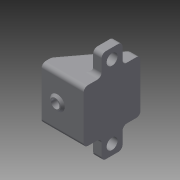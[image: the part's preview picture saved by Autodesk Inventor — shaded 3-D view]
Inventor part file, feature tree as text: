
AUTODESK INVENTOR PART (.ipt)
format: ipt  version: 2015 (Build 190159000, 159)  size: 220,672 bytes
history: native  units: mm
features: sketch x8, extrude x4, fillet x4, hole x2, plane x2, mirror x2, projected_geometry x2, loft x1, chamfer x1
ambient origin geometry x8: Origin, YZ Plane, XZ Plane, XY Plane, X Axis, Y Axis, Z Axis, Center Point
bodies: Solid1 (feature_tree)
feature tree (26):
  extrude  "Extrusion1"  Depth=25.0mm
  extrude  "Extrusion2"  Depth=5.0mm
  hole  "Hole1"  [1 undecoded]
  sketch  "Sketch4"  dims[d7=4.0mm d8=6.0mm d9=10.1mm d10=4.5mm d11=90.0deg d12=8.0mm d13=20.594885mm d14=5.0mm]
  plane  "Work Plane1"
  loft  "Loft1"
  fillet  "Fillet1"  [1 undecoded]
  mirror  "Mirror1"
  fillet  "Fillet2"  Radius=2.0mm
  extrude  "Extrusion3"  Depth=7.0mm
  chamfer  "Chamfer1"  Distance=1.0mm
  extrude  "Extrusion4"  Depth=4.0mm TaperAngle=0.0deg
  fillet  "Fillet3"  Radius=10.0mm
  hole  "Hole2"  [1 undecoded]
  plane  "Work Plane2"
  mirror  "Mirror2"
  fillet  "Fillet4"  Radius=2.0mm
  sketch  "Sketch1"  dims[d0=20.0mm d1=25.0mm]
  sketch  "Sketch2"  dims[d2=7.0mm d3=0.0mm d4=5.0mm]
  sketch  "Sketch3"  dims[d5=20.0mm d6=0.0mm]
  projected_geometry  "Projected Loop1"
  projected_geometry  "Projected Loop2"
  sketch  "Sketch5"  dims[d15=5.0mm d16=0.0mm d17=90.0deg d18=0.0mm d19=90.0deg d20=2.0mm]
  sketch  "Sketch6"  dims[d21=2.0mm d22=7.0mm d23=1.0mm d24=0.0mm]
  sketch  "Sketch7"  dims[d25=1.0mm d26=2.0mm d27=45.0deg d28=4.0mm d29=0.0mm d30=10.0mm]
  sketch  "Sketch8"  dims[d31=11.0mm d32=2.0mm d33=5.2mm d34=6.0mm d35=7.1mm d36=4.0mm d37=90.0deg d38=8.0mm d39=20.594885mm d40=2.0mm]
note: 3 required parameter values undecoded (feature->parameter linkage not recoverable at this tier; creation-order binding heuristic only, values carry confidence <= 0.55)
